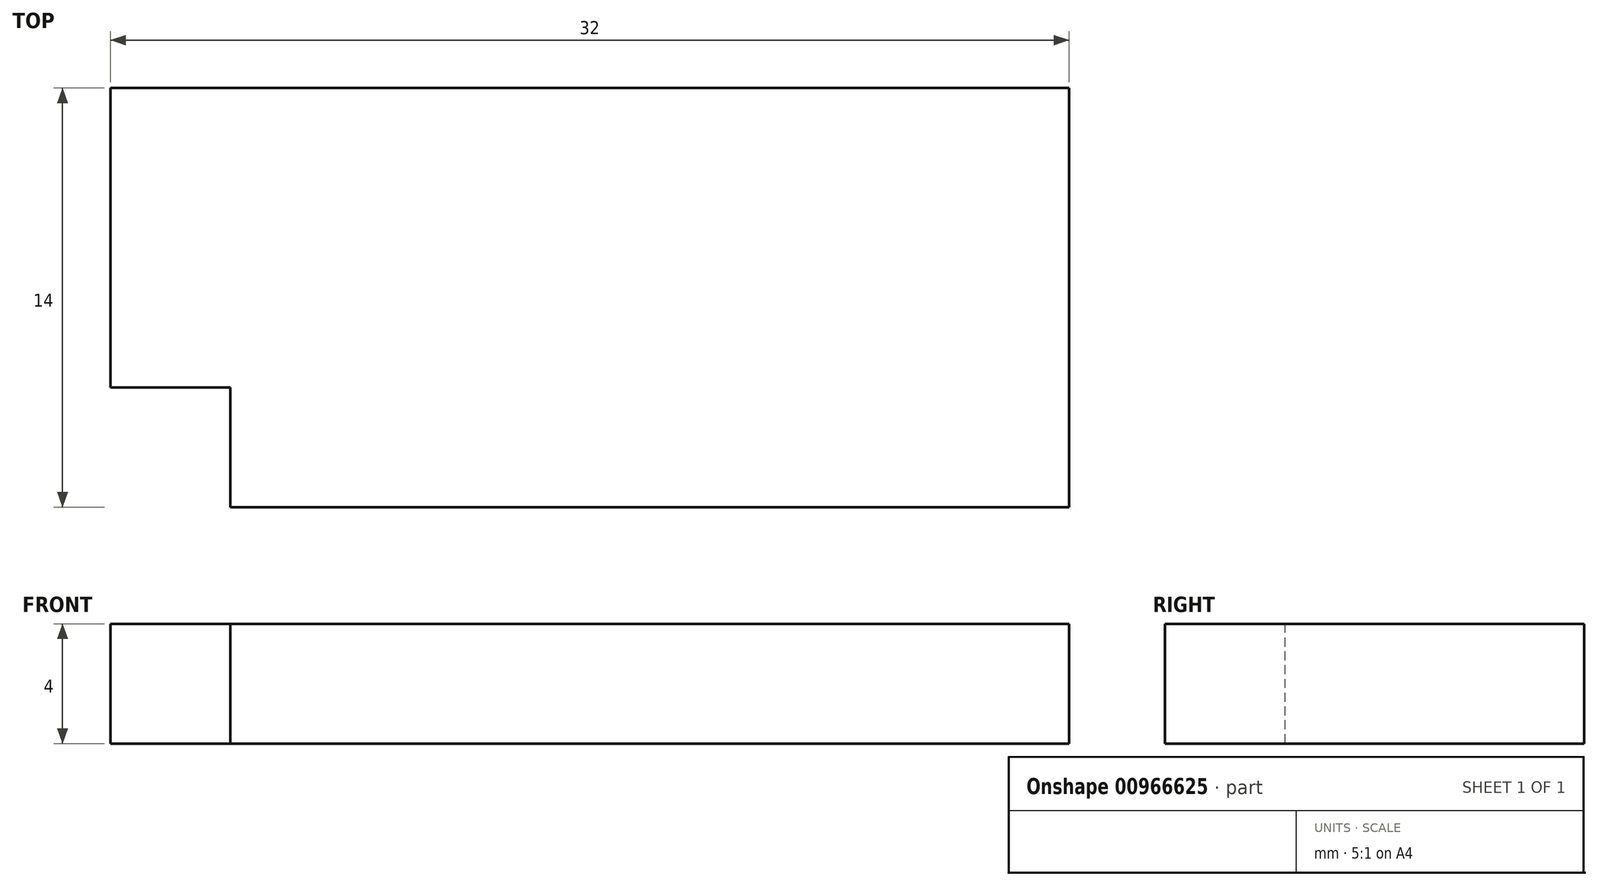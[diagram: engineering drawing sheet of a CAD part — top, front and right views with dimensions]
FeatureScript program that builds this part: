
annotation { "Feature Type Name" : "Feature", "Feature Type Description" : "" }
export const myFeature = defineFeature(function(context is Context, id is Id, definition is map)
    precondition{}
    {
        {
            var Q0;
            Q0=qCreatedBy(makeId("Top.planeOp"),FACE);
            var sketch = newSketch(context, id + "F0", { "sketchPlane" : qUnion([Q0])});
            skLineSegment(sketch, "E0.bottom", {"start": v(16, 5) * mm, "end": v(-16, 5) * mm});
            skLineSegment(sketch, "E0.top", {"start": v(16, -5) * mm, "end": v(-16, -5) * mm});
            skLineSegment(sketch, "E0.left", {"start": v(16, 5) * mm, "end": v(16, -5) * mm});
            skLineSegment(sketch, "E0.right", {"start": v(-16, 5) * mm, "end": v(-16, -5) * mm});
            skPoint(sketch, "E0.middle", {"position": v(0, 0) * mm});
            skLineSegment(sketch, "E1", {"start": v(-12, -5) * mm, "end": v(-12, -9) * mm});
            skLineSegment(sketch, "E2", {"start": v(-12, -9) * mm, "end": v(16, -9) * mm});
            skLineSegment(sketch, "E3", {"start": v(16, -9) * mm, "end": v(16, -5) * mm});
            skSolve(sketch);
        }
        {
            var Q0;
            Q0=makeQuery(id+"F0.imprint","IMPRINT",FACE,{"disambiguationData":[TD([[makeQuery(id+"F0.imprint","IMPRINT",EDGE,{"derivedFrom":sQuery(id+"F0.wireOp",EDGE,"E0.bottom")}),1.0]])]});
            var Q1;
            {var subQ2=sQuery(id+"F0.wireOp",EDGE,"E1");Q1=makeQuery(id+"F0.imprint","IMPRINT",FACE,{"disambiguationData":[TD([[makeQuery(id+"F0.imprint","IMPRINT",EDGE,{"derivedFrom":subQ2}),1.0]])]});}
            extrude(context, id + "F1", {"entities" : qUnion([Q0, Q1]), "depth" : 4 * mm, "offsetDistance" : 25 * mm});
        }
    });
